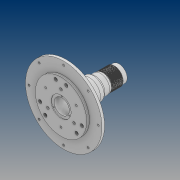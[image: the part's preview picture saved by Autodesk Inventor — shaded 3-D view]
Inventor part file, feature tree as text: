
AUTODESK INVENTOR PART (.ipt)
format: ipt  version: 2021 (Build 250183000, 183)  size: 1,886,720 bytes
history: native  units: in
note: dims shown in document units (in); Inventor stores cm internally (conversion verified against a paired STEP export)
features: thread x17, sketch x3, extrude x2, pattern_circular x2, revolve x1
ambient origin geometry x8: Origin, YZ Plane, XZ Plane, XY Plane, X Axis, Y Axis, Z Axis, Center Point
bodies: Solid2 (feature_tree), Solid1 (feature_tree)
feature tree (25):
  extrude  "Extrusion1"  Depth=0.1969in TaperAngle=0.0deg
  extrude  "Extrusion2"  Depth=0.315in
  pattern_circular  "Circular Pattern1"  Count=3  [1 undecoded]
  thread  "Thread1"  [1 undecoded]
  thread  "Thread3"  [1 undecoded]
  thread  "Thread6"  [1 undecoded]
  thread  "Thread7"  [1 undecoded]
  thread  "Thread8"  [1 undecoded]
  thread  "Thread9"  [1 undecoded]
  thread  "Thread10"  [1 undecoded]
  thread  "Thread11"  [1 undecoded]
  thread  "Thread12"  [1 undecoded]
  thread  "Thread13"  [1 undecoded]
  thread  "Thread14"  [1 undecoded]
  thread  "Thread15"  [1 undecoded]
  thread  "Thread16"  [1 undecoded]
  thread  "Thread17"  [1 undecoded]
  thread  "Thread18"  [1 undecoded]
  thread  "Thread19"  [1 undecoded]
  thread  "Thread20"  [1 undecoded]
  revolve  "Revolution3"  [1 undecoded]
  pattern_circular  "Circular Pattern3"  Angle=90.0deg  [1 undecoded]
  sketch  "Sketch1"  dims[d1=6.0197in d2=0.1969in d3=0.0in]
  sketch  "Sketch2"  dims[d4=5.2362in d5=0.315in]
  sketch  "Sketch6"  dims[d6=0.315in d7=0.0in d9=1.1811in d10=2.4737in d12=0.315in d13=0.0in d16=0.315in d17=0.0in d22=0.315in d23=0.0in d24=0.7874in d25=0.0in d26=0.7874in d27=0.0in d28=0.7874in d29=0.0in d30=0.7874in d31=0.0in d32=0.7874in d33=0.0in d34=0.7874in d35=0.0in d36=0.7874in d37=0.0in d38=0.7874in d39=0.0in d40=1.5748in d41=0.0in d42=1.5748in d43=0.0in d44=1.5748in d45=0.0in d46=1.5748in d47=0.0in d48=1.5748in d49=0.0in d50=1.5748in d51=0.0in d57=0.0in d58=90.0deg d59=1.1811in d60=2.4737in]
note: 20 required parameter values undecoded (feature->parameter linkage not recoverable at this tier; creation-order binding heuristic only, values carry confidence <= 0.55)